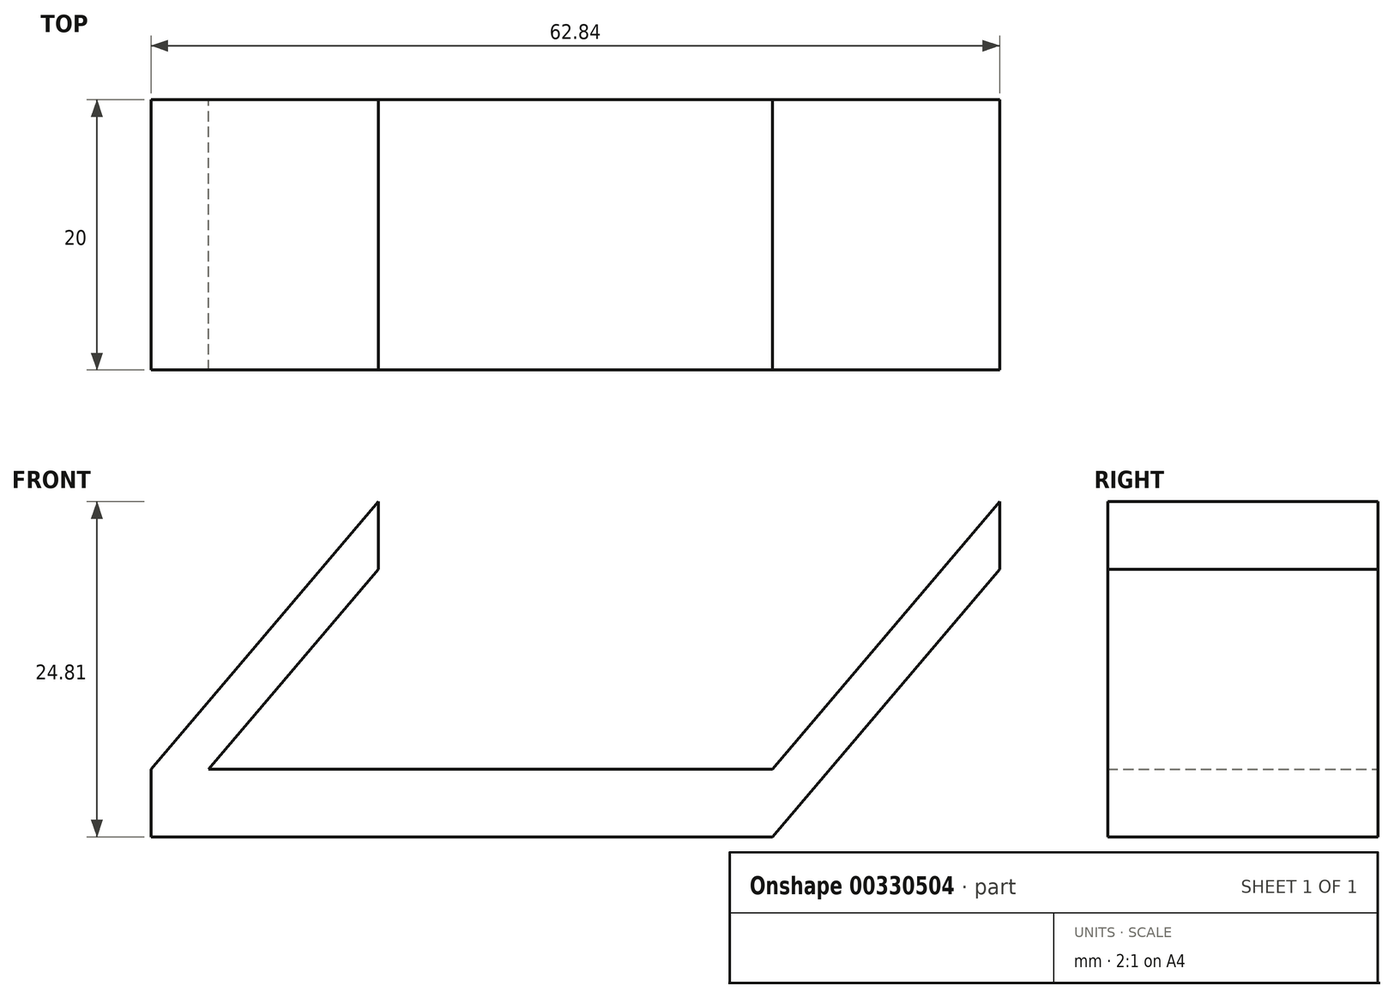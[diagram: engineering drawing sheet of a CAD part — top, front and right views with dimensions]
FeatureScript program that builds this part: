
annotation { "Feature Type Name" : "Feature", "Feature Type Description" : "" }
export const myFeature = defineFeature(function(context is Context, id is Id, definition is map)
    precondition{}
    {
        {
            var Q0;
            Q0=qCreatedBy(makeId("Front.planeOp"),FACE);
            var sketch = newSketch(context, id + "F0", { "sketchPlane" : qUnion([Q0])});
            skLineSegment(sketch, "E0", {"start": v(0, 0) * mm, "end": v(-46, 0) * mm});
            skLineSegment(sketch, "E1", {"start": v(-46, 0) * mm, "end": v(0, 0) * mm});
            skLineSegment(sketch, "E2", {"start": v(0, 0) * mm, "end": v(0, -5) * mm});
            skLineSegment(sketch, "E3", {"start": v(0, -5) * mm, "end": v(-46, -5) * mm});
            skLineSegment(sketch, "E4", {"start": v(-46, -5) * mm, "end": v(-46, 0) * mm});
            skLineSegment(sketch, "E5", {"start": v(0, 0) * mm, "end": v(16.84, 19.81) * mm});
            skLineSegment(sketch, "E6", {"start": v(16.84, 19.81) * mm, "end": v(0, 0) * mm});
            skLineSegment(sketch, "E7", {"start": v(-46, 0) * mm, "end": v(-29.16, 19.81) * mm});
            skLineSegment(sketch, "E8", {"start": v(-29.16, 19.81) * mm, "end": v(-29.16, 14.81) * mm});
            skLineSegment(sketch, "E9", {"start": v(-46, -5) * mm, "end": v(-29.16, 14.81) * mm});
            skLineSegment(sketch, "E10", {"start": v(16.84, 19.81) * mm, "end": v(16.84, 14.81) * mm});
            skLineSegment(sketch, "E11", {"start": v(16.84, 14.81) * mm, "end": v(0, -5) * mm});
            skSolve(sketch);
        }
        {
            var Q0;
            {var subQ0=sQuery(id+"F0.wireOp",EDGE,"E4");Q0=makeQuery(id+"F0.imprint","IMPRINT",FACE,{"disambiguationData":[TD([[makeQuery(id+"F0.imprint","IMPRINT",EDGE,{"derivedFrom":subQ0}),-1.0]])]});}
            var Q1;
            {var subQ0=sQuery(id+"F0.wireOp",EDGE,"E2");Q1=makeQuery(id+"F0.imprint","IMPRINT",FACE,{"disambiguationData":[TD([[makeQuery(id+"F0.imprint","IMPRINT",EDGE,{"derivedFrom":subQ0}),-1.0]])]});}
            var Q2;
            {var subQ0=sQuery(id+"F0.wireOp",EDGE,"E7");Q2=makeQuery(id+"F0.imprint","IMPRINT",FACE,{"disambiguationData":[TD([[makeQuery(id+"F0.imprint","IMPRINT",EDGE,{"derivedFrom":subQ0}),-1.0]])]});}
            var Q3;
            Q3=makeQuery(id+"F0.imprint","IMPRINT",FACE,{"disambiguationData":[TD([[makeQuery(id+"F0.imprint","IMPRINT",EDGE,{"derivedFrom":sQuery(id+"F0.wireOp",EDGE,"E2")}),1.0]])]});
            extrude(context, id + "F1", {"entities" : qUnion([Q0, Q1, Q2, Q3]), "depth" : 20 * mm});
        }
    });
